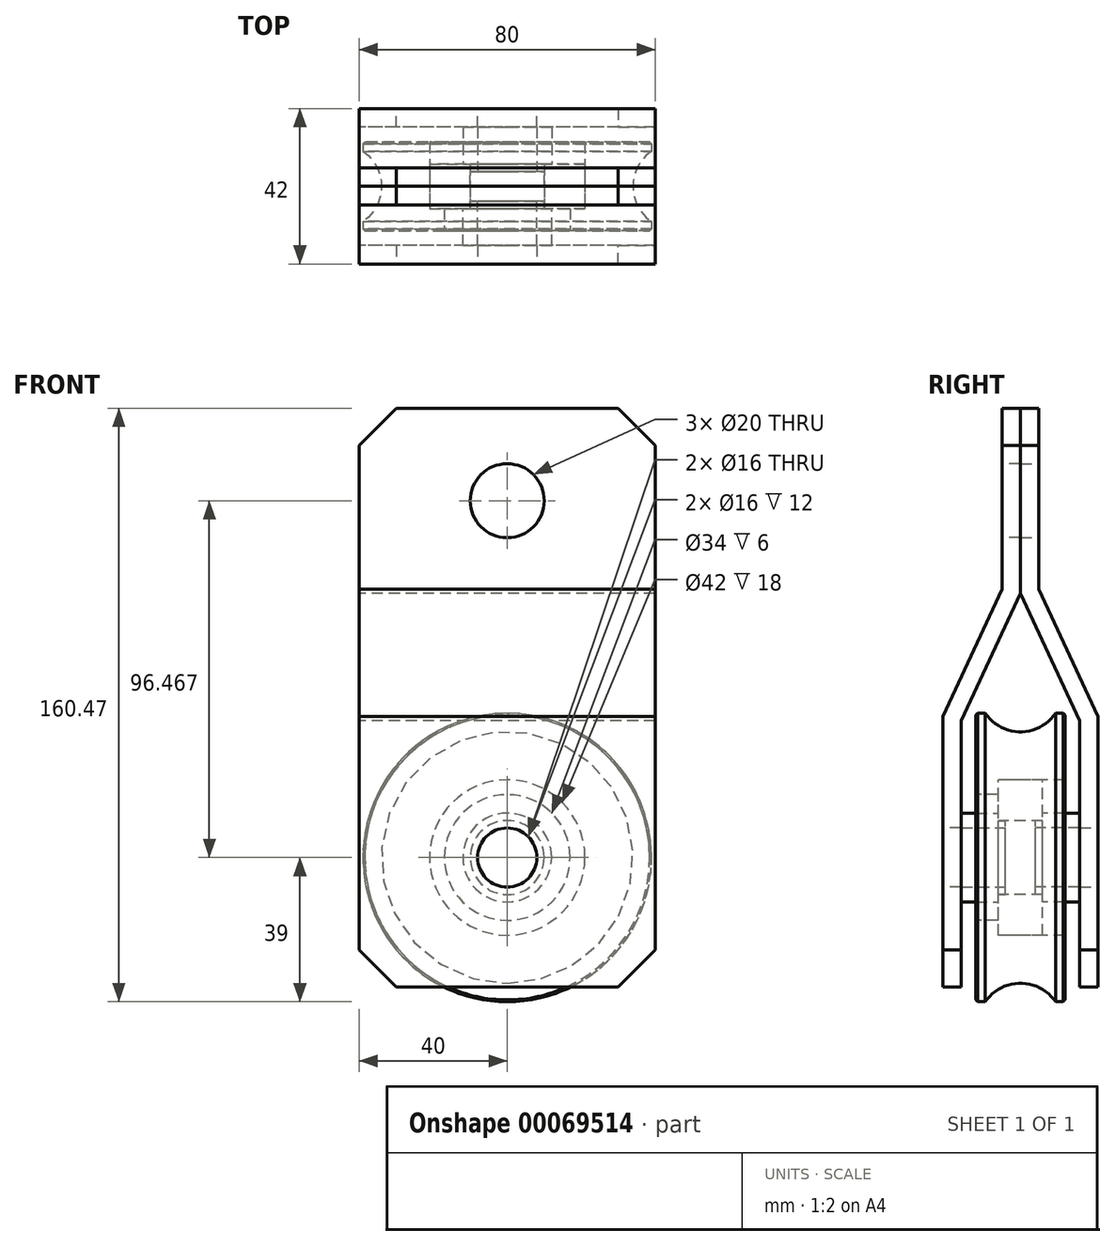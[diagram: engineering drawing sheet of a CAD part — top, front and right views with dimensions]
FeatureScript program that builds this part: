
annotation { "Feature Type Name" : "Feature", "Feature Type Description" : "" }
export const myFeature = defineFeature(function(context is Context, id is Id, definition is map)
    precondition{}
    {
        {
            var Q0;
            Q0=qCreatedBy(makeId("Right.planeOp"),FACE);
            var sketch = newSketch(context, id + "F0", { "sketchPlane" : qUnion([Q0])});
            skLineSegment(sketch, "E0", {"start": v(-24.2, 0) * mm, "end": v(23.6, 0) * mm, "construction": true});
            skLineSegment(sketch, "E1", {"start": v(-12, 17) * mm, "end": v(12, 17) * mm});
            skLineSegment(sketch, "E2", {"start": v(12, 17) * mm, "end": v(12, 39) * mm});
            skLineSegment(sketch, "E3", {"start": v(12, 39) * mm, "end": v(9.5, 39) * mm});
            skLineSegment(sketch, "E4.MirrorCS", {"start": v(-12, 39) * mm, "end": v(-9.5, 39) * mm});
            skLineSegment(sketch, "E5.MirrorCS", {"start": v(-12, 17) * mm, "end": v(-12, 39) * mm});
            skCircle(sketch, "E6", {"center": v(0, 45.53) * mm, "radius": 11.53 * mm});
            skPoint(sketch, "E6.centerSnap0", {"position": v(0, 17) * mm});
            skLineSegment(sketch, "E7", {"start": v(-6, 17) * mm, "end": v(-6, 21) * mm});
            skLineSegment(sketch, "E8", {"start": v(-6, 21) * mm, "end": v(12, 21) * mm});
            skPoint(sketch, "E8.endSnap0", {"position": v(12, 28) * mm});
            skSolve(sketch);
        }
        {
            var Q0;
            {var subQ1=sQuery(id+"F0.wireOp",EDGE,"E3");Q0=makeQuery(id+"F0.imprint","IMPRINT",FACE,{"disambiguationData":[TD([[makeQuery(id+"F0.imprint","IMPRINT",EDGE,{"derivedFrom":subQ1}),1.0]])]});}
            var Q1;
            Q1=sQuery(id+"F0.wireOp",EDGE,"E0");
            revolve(context, id + "F1", {"entities" : qUnion([Q0]), "axis" : qUnion([Q1]), "revolveType" : RevolveType.FULL});
        }
        {
            var Q0;
            Q0=makeQuery(id+"F1.opRevolve","SWEPT_EDGE",EDGE,{"disambiguationData":[OSD([sQuery(id+"F0.wireOp",EDGE,"E2"),sQuery(id+"F0.wireOp",EDGE,"E3")])]});
            var Q1;
            Q1=makeQuery(id+"F1.opRevolve","SWEPT_EDGE",EDGE,{"disambiguationData":[OSD([sQuery(id+"F0.wireOp",EDGE,"E4.MirrorCS"),sQuery(id+"F0.wireOp",EDGE,"E5.MirrorCS")])]});
            chamfer(context, id + "F2", {"entities" : qUnion([Q0, Q1]), "width" : 0.5 * mm, "tangentPropagation" : true});
        }
        {
            var Q0;
            Q0=qCreatedBy(makeId("Right.planeOp"),FACE);
            var sketch = newSketch(context, id + "F3", { "sketchPlane" : qUnion([Q0])});
            skLineSegment(sketch, "E9", {"start": v(-6, 21) * mm, "end": v(6, 21) * mm});
            skLineSegment(sketch, "E10.0.0", {"start": v(-6, 21) * mm, "end": v(-6, 10) * mm, "construction": true});
            skLineSegment(sketch, "E11.top", {"start": v(-6, 10) * mm, "end": v(6, 10) * mm});
            skLineSegment(sketch, "E11.left", {"start": v(-6, 21) * mm, "end": v(-6, 10) * mm});
            skLineSegment(sketch, "E11.right", {"start": v(6, 21) * mm, "end": v(6, 10) * mm});
            skPoint(sketch, "E12.orphan", {"position": v(-6, -21) * mm});
            skLineSegment(sketch, "E13", {"start": v(-29.1, 0) * mm, "end": v(25.21, 0) * mm, "construction": true});
            skSolve(sketch);
        }
        {
            var Q0;
            Q0 = qSketchRegion(id + "F3", true);
            var Q1;
            Q1=sQuery(id+"F3.wireOp",EDGE,"E13");
            revolve(context, id + "F4", {"entities" : qUnion([Q0]), "axis" : qUnion([Q1]), "revolveType" : RevolveType.FULL});
        }
        {
            var Q0;
            Q0=qCreatedBy(makeId("Right.planeOp"),FACE);
            var sketch = newSketch(context, id + "F5", { "sketchPlane" : qUnion([Q0])});
            skLineSegment(sketch, "E14", {"start": v(4, 10) * mm, "end": v(6, 10) * mm});
            skLineSegment(sketch, "E15.0.0", {"start": v(6, 12) * mm, "end": v(6, 10) * mm});
            skLineSegment(sketch, "E16", {"start": v(6, 12) * mm, "end": v(16, 12) * mm});
            skLineSegment(sketch, "E17", {"start": v(16, 12) * mm, "end": v(16, 8) * mm});
            skLineSegment(sketch, "E18", {"start": v(16, 8) * mm, "end": v(4, 8) * mm});
            skLineSegment(sketch, "E19", {"start": v(4, 8) * mm, "end": v(4, 10) * mm});
            skPoint(sketch, "E20.orphan", {"position": v(6, 21) * mm});
            skPoint(sketch, "E21.trimOffspring.end.orphan", {"position": v(6, -21) * mm});
            skLineSegment(sketch, "E22", {"start": v(-22.49, 0) * mm, "end": v(21.7, 0) * mm, "construction": true});
            skSolve(sketch);
        }
        {
            var Q0;
            Q0 = qSketchRegion(id + "F5", true);
            var Q1;
            Q1=sQuery(id+"F5.wireOp",EDGE,"E22");
            revolve(context, id + "F6", {"entities" : qUnion([Q0]), "axis" : qUnion([Q1]), "revolveType" : RevolveType.FULL});
        }
        {
            var Q0;
            Q0=makeQuery(id+"F6.opRevolve","SWEPT_BODY",BODY,{"disambiguationData":[OSD([sQuery(id+"F5.wireOp",EDGE,"E14"),sQuery(id+"F5.wireOp",EDGE,"E15.0.0"),sQuery(id+"F5.wireOp",EDGE,"E16"),sQuery(id+"F5.wireOp",EDGE,"E17"),sQuery(id+"F5.wireOp",EDGE,"E18"),sQuery(id+"F5.wireOp",EDGE,"E19")])]});
            var Q1;
            Q1=qCreatedBy(makeId("Front.planeOp"),FACE);
            mirror(context, id + "F7", {"entities" : qUnion([Q0]), "mirrorPlane" : qUnion([Q1])});
        }
        {
            var Q0;
            Q0=qCreatedBy(makeId("Right.planeOp"),FACE);
            var sketch = newSketch(context, id + "F8", { "sketchPlane" : qUnion([Q0])});
            skLineSegment(sketch, "E23", {"start": v(16, 37) * mm, "end": v(0, 71.47) * mm});
            skLineSegment(sketch, "E24", {"start": v(0, 71.47) * mm, "end": v(0, 121.47) * mm});
            skLineSegment(sketch, "E25", {"start": v(0, 121.47) * mm, "end": v(5, 121.47) * mm});
            skLineSegment(sketch, "E26", {"start": v(16, 37) * mm, "end": v(16, -35) * mm});
            skLineSegment(sketch, "E27.0", {"start": v(5, 72.57) * mm, "end": v(5, 121.47) * mm});
            skLineSegment(sketch, "E27.1", {"start": v(21, 38.1) * mm, "end": v(5, 72.57) * mm});
            skLineSegment(sketch, "E27.3", {"start": v(21, 38.1) * mm, "end": v(21, -35) * mm});
            skLineSegment(sketch, "E28", {"start": v(16, -35) * mm, "end": v(21, -35) * mm});
            skSolve(sketch);
        }
        {
            var Q0;
            Q0 = qSketchRegion(id + "F8", true);
            extrude(context, id + "F9", {"entities" : qUnion([Q0]), "endBound" : BoundingType.SYMMETRIC, "depth" : 80 * mm});
        }
        {
            var Q0;
            Q0=makeQuery(id+"F9.opExtrude","SWEPT_FACE",FACE,{"disambiguationData":[OSD([sQuery(id+"F8.wireOp",EDGE,"E27.3")])]});
            var sketch = newSketch(context, id + "F10", { "sketchPlane" : qUnion([Q0])});
            skCircle(sketch, "E29", {"center": v(0, 0) * mm, "radius": 8 * mm});
            skCircle(sketch, "E30", {"center": v(0, 96.47) * mm, "radius": 10 * mm});
            skPoint(sketch, "E30.centerSnap0", {"position": v(0, 38.1) * mm});
            skSolve(sketch);
        }
        {
            var Q0;
            Q0=makeQuery(id+"F10.imprint","IMPRINT",FACE,{"disambiguationData":[TD([[makeQuery(id+"F10.imprint","IMPRINT",EDGE,{"derivedFrom":sQuery(id+"F10.wireOp",EDGE,"E29")}),1.0]])]});
            var Q1;
            Q1=makeQuery(id+"F10.imprint","IMPRINT",FACE,{"disambiguationData":[TD([[makeQuery(id+"F10.imprint","IMPRINT",EDGE,{"derivedFrom":sQuery(id+"F10.wireOp",EDGE,"E30")}),1.0]])]});
            extrude(context, id + "F11", {"entities" : qUnion([Q0, Q1]), "operationType" : NewBodyOperationType.REMOVE, "endBound" : BoundingType.THROUGH_ALL, "oppositeDirection" : true, "depth" : 25 * mm});
        }
        {
            var Q0;
            Q0=makeQuery(id+"F9.opExtrude","CAP_EDGE",EDGE,{"disambiguationData":[OSD([sQuery(id+"F8.wireOp",EDGE,"E25")])],"isStart":false});
            var Q1;
            Q1=makeQuery(id+"F9.opExtrude","CAP_EDGE",EDGE,{"disambiguationData":[OSD([sQuery(id+"F8.wireOp",EDGE,"E25")])],"isStart":true});
            var Q2;
            Q2=makeQuery(id+"F9.opExtrude","CAP_EDGE",EDGE,{"disambiguationData":[OSD([sQuery(id+"F8.wireOp",EDGE,"E28")])],"isStart":false});
            var Q3;
            Q3=makeQuery(id+"F9.opExtrude","CAP_EDGE",EDGE,{"disambiguationData":[OSD([sQuery(id+"F8.wireOp",EDGE,"E28")])],"isStart":true});
            chamfer(context, id + "F12", {"entities" : qUnion([Q0, Q1, Q2, Q3]), "width" : 10 * mm, "tangentPropagation" : true});
        }
        {
            var Q0;
            Q0=makeQuery(id+"F9.opExtrude","SWEPT_BODY",BODY,{"disambiguationData":[OSD([sQuery(id+"F8.wireOp",EDGE,"E23"),sQuery(id+"F8.wireOp",EDGE,"E24"),sQuery(id+"F8.wireOp",EDGE,"E25"),sQuery(id+"F8.wireOp",EDGE,"E26"),sQuery(id+"F8.wireOp",EDGE,"E27.0"),sQuery(id+"F8.wireOp",EDGE,"E27.1"),sQuery(id+"F8.wireOp",EDGE,"E27.3"),sQuery(id+"F8.wireOp",EDGE,"E28")])]});
            var Q1;
            Q1=qCreatedBy(makeId("Front.planeOp"),FACE);
            mirror(context, id + "F13", {"entities" : qUnion([Q0]), "mirrorPlane" : qUnion([Q1])});
        }
    });
